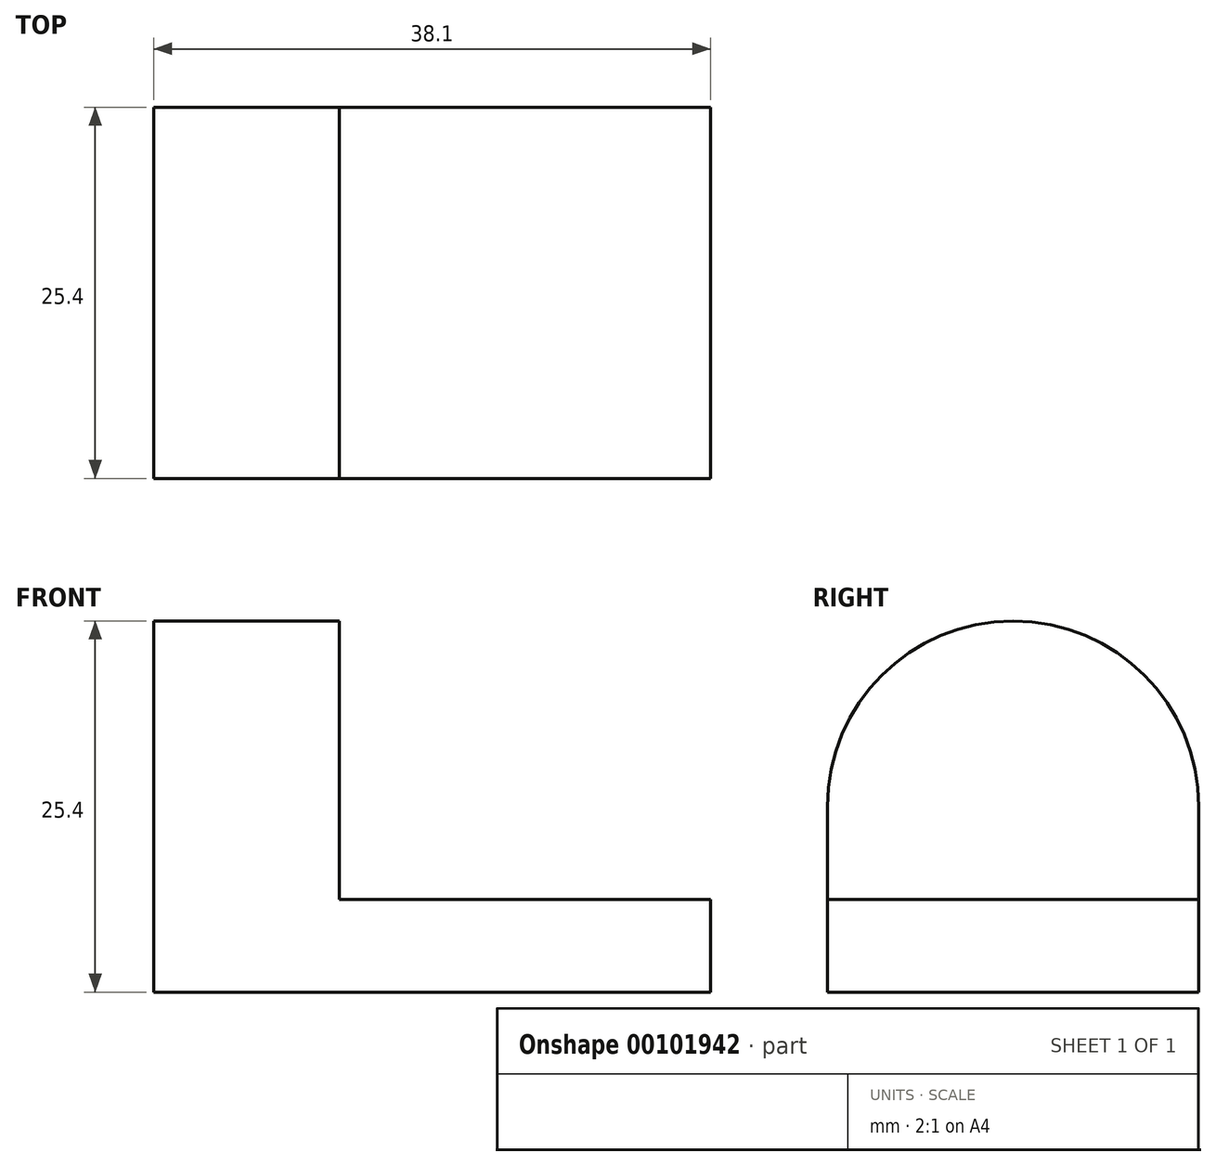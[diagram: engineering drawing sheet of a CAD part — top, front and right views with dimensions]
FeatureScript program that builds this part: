
annotation { "Feature Type Name" : "Feature", "Feature Type Description" : "" }
export const myFeature = defineFeature(function(context is Context, id is Id, definition is map)
    precondition{}
    {
        {
            var Q0;
            Q0=qCreatedBy(makeId("Right.planeOp"),FACE);
            var sketch = newSketch(context, id + "F0", { "sketchPlane" : qUnion([Q0])});
            skLineSegment(sketch, "E0", {"start": v(-12.7, 0) * mm, "end": v(12.7, 0) * mm});
            skLineSegment(sketch, "E1", {"start": v(12.7, 0) * mm, "end": v(12.7, 6.35) * mm});
            skLineSegment(sketch, "E2", {"start": v(12.7, 6.35) * mm, "end": v(-12.7, 6.35) * mm});
            skLineSegment(sketch, "E3", {"start": v(-12.7, 6.35) * mm, "end": v(-12.7, 0) * mm});
            skLineSegment(sketch, "E4", {"start": v(-12.7, 6.35) * mm, "end": v(-12.7, 12.7) * mm});
            skLineSegment(sketch, "E5", {"start": v(-12.7, 12.7) * mm, "end": v(12.7, 12.7) * mm});
            skLineSegment(sketch, "E6", {"start": v(12.7, 12.7) * mm, "end": v(12.7, 6.35) * mm});
            skArc(sketch, "E7", {"start": v(12.7, 12.7) * mm, "mid": v(0, 25.4) * mm, "end": v(-12.7, 12.7) * mm});
            skSolve(sketch);
        }
        {
            var Q0;
            Q0 = qSketchRegion(id + "F0", true);
            extrude(context, id + "F1", {"entities" : qUnion([Q0]), "depth" : 38.1 * mm});
        }
        {
            var Q0;
            Q0=makeQuery(id+"F1.opExtrude","CAP_FACE",FACE,{"disambiguationData":[OSD([sQuery(id+"F0.wireOp",EDGE,"E0"),sQuery(id+"F0.wireOp",EDGE,"E1"),sQuery(id+"F0.wireOp",EDGE,"E3"),sQuery(id+"F0.wireOp",EDGE,"E4"),sQuery(id+"F0.wireOp",EDGE,"E6"),sQuery(id+"F0.wireOp",EDGE,"E7")])],"isStart":false});
            var sketch = newSketch(context, id + "F2", { "sketchPlane" : qUnion([Q0])});
            skLineSegment(sketch, "E8", {"start": v(-12.7, 6.35) * mm, "end": v(12.7, 6.35) * mm});
            skArc(sketch, "E9", {"start": v(12.7, 6.35) * mm, "mid": v(0, 26.9) * mm, "end": v(-12.7, 6.35) * mm});
            skSolve(sketch);
        }
        {
            var Q0;
            {var subQ0=sQuery(id+"F2.wireOp",EDGE,"E8");Q0=makeQuery(id+"F2.imprint","IMPRINT",FACE,{"disambiguationData":[TD([[makeQuery(id+"F2.imprint","IMPRINT",EDGE,{"derivedFrom":subQ0}),1.0]])]});}
            extrude(context, id + "F3", {"entities" : qUnion([Q0]), "operationType" : NewBodyOperationType.REMOVE, "oppositeDirection" : true, "depth" : 25.4 * mm});
        }
    });
